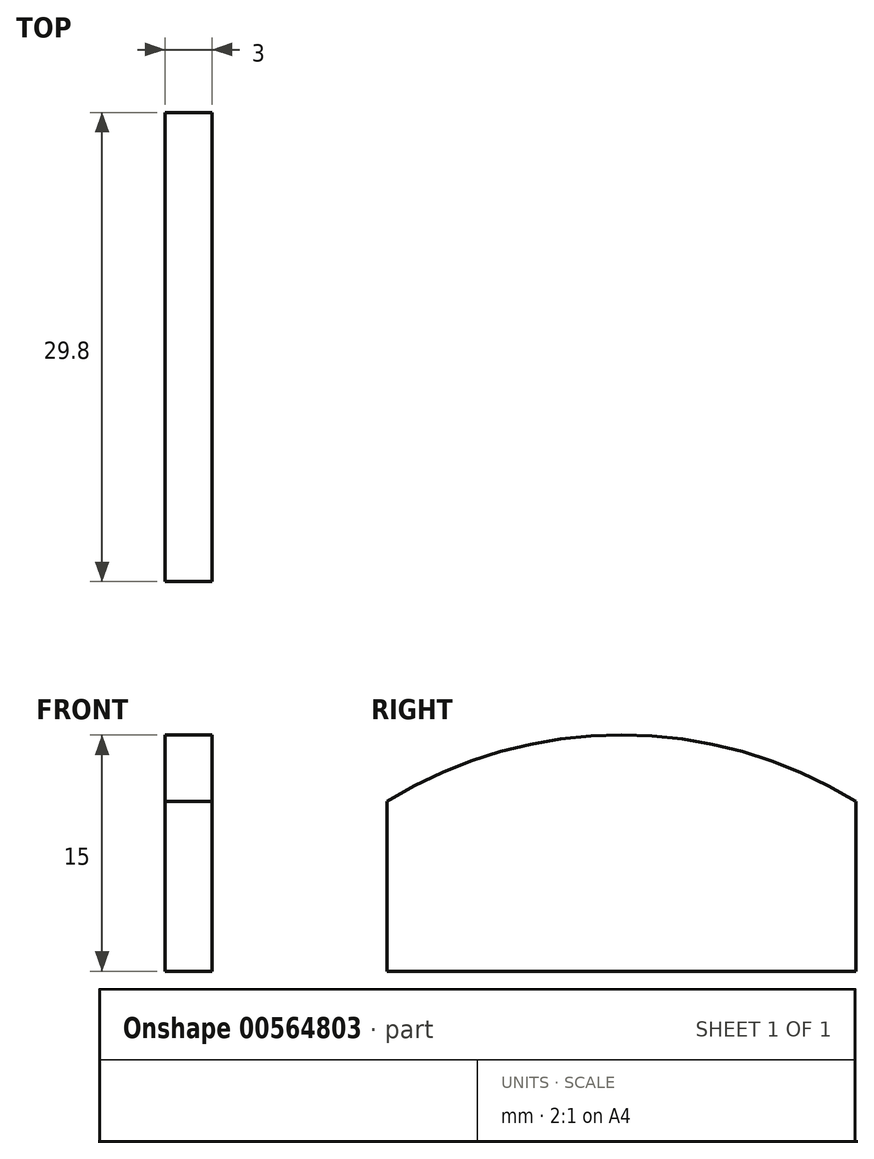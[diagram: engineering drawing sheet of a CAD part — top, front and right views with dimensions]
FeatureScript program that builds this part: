
annotation { "Feature Type Name" : "Feature", "Feature Type Description" : "" }
export const myFeature = defineFeature(function(context is Context, id is Id, definition is map)
    precondition{}
    {
        {
            var Q0;
            Q0=qCreatedBy(makeId("Right.planeOp"),FACE);
            var sketch = newSketch(context, id + "F0", { "sketchPlane" : qUnion([Q0])});
            skLineSegment(sketch, "E0.bottom", {"start": v(-14.9, 0) * mm, "end": v(14.9, 0) * mm});
            skLineSegment(sketch, "E0.top", {"start": v(-14.9, 15) * mm, "end": v(14.9, 15) * mm});
            skLineSegment(sketch, "E0.left", {"start": v(-14.9, 0) * mm, "end": v(-14.9, 15) * mm});
            skLineSegment(sketch, "E0.right", {"start": v(14.9, 0) * mm, "end": v(14.9, 15) * mm});
            skPoint(sketch, "E1", {"position": v(0, 0) * mm});
            skCircle(sketch, "E2", {"center": v(0, -13.5) * mm, "radius": 28.5 * mm});
            skSolve(sketch);
        }
        {
            var Q0;
            Q0=makeQuery(id+"F0.imprint","IMPRINT",FACE,{"disambiguationData":[TD([[makeQuery(id+"F0.imprint","IMPRINT",EDGE,{"derivedFrom":sQuery(id+"F0.wireOp",EDGE,"E0.bottom")}),1.0]])]});
            extrude(context, id + "F1", {"entities" : qUnion([Q0]), "depth" : 3 * mm, "offsetDistance" : 25 * mm});
        }
    });
